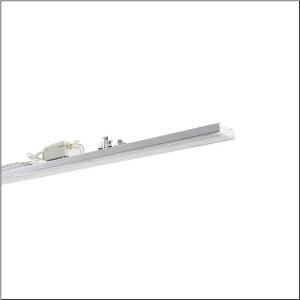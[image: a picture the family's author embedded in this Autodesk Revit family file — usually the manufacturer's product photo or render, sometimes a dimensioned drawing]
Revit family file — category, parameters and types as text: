
# Revit family: licross_r__21_recessed_mo_52tl12dn4axg3c_4f99
name_source: partatom
category: Lighting Fixtures
units: mm (PartAtom-declared; Revit-internal decimal feet)

## family parameters
Cut with Voids When Loaded = No
Host = Face
Light Source = No
Part Type = Normal
Room Calculation Point = No
Round Connector Dimension = Use Diameter
Shared = No

## types (1)
- --- (1 x LED, 950 lm, 6.7 W, 4000K)
    Apparent Load = 7 VA
    CIE Flux Codes = 72 92 99 100 100
    Color Rendering = 80
    Color Temperature = 4000K
    Default Elevation = 1800 mm
    Description = Licross® 21 Recessed MO, luminaire insert, of sheet steel, galvanised, coil coated, white, length: 1.500mm, width: 66mm, height: 67mm, LED rated luminous flux: 10.280lm, light colour: 840, control gear: DALI 2, with plug, 6-pole, with phase selection, for trunking rail, 14-core, mains connection: 220..240V, AC, 50/60Hz, rated input power: 62W, halogen-free wiring, for emergency light function, for trunking rail, 14-core, converter,control gear: single battery element, battery: LiFeP04, 9Ah, primary optical cover: cover, of PMMA, light emission: direct distribution, primary light characteristic: symmetric, protection rating (complete): IP40, insulation class (complete): insulation class I (protective earthing), certification: CE, UKCA, protection symbol: D if used in an environment without relevant dust loads with corresponding accessories, impact resistance: IK06, permissible ambient temperature for indoor applications: +5..+35°C, standard: EN 60598-2-22, LABS conformity tested according to VDMA 24364:2018-05, reducing of maximum allowable ambient temperature of 5°C with ceiling mounting, corresponds to IFS (International Featured Standards) requirements for safety and quality in the food industry, packaging unit: 1 piece
    Height = 58 mm
    Lamp = 1 x LED
    Lamp Light Flux = 950 lm
    Lamp Power = 6.7 W
    Lamp count = 1
    Length = 1500 mm
    Luminous efficacy = 142 lm/W
    Manufacturer = Siteco
    ModVariant = No
    Model = 52TL12DN4AXG3C
    Mounting Place = Ceiling
    Mounting Type = Pendant
    Number of Poles = 1
    OnlyDefault = Yes
    Power Factor = 1
    Product Name = Licross® 21 Recessed MO
    Product group = luminaire insert
    ProductGroupID = 901
    Protection Class = Protection class I
    Protection Degree = IP 40
    RLX_Detail_Level = 1
    RLX_Emergency_Light_Flux = 0 lm
    RLX_Emergency_Type = 0
    RLX_Emergency_Type_DB = No
    RlxData = <blob elided: 24993 chars, md5=75ffac7b>
    Socket = socket
    Standby Power = 0 W
    System Light Flux = 950 lm
    System Power = 7 W
    Type Comments = : emergency light operation: 3 h
    Type Image = l_1296930.jpg
    URL = http://relux.com
    VarID = @adj_040183
    Voltage = 0 V
    Weight = 0.00 kg
    Width = 66 mm

## geometry (parser evidence)
native form markers: Blend x4, Sweep x9
no freeform markers — native parametric forms only
